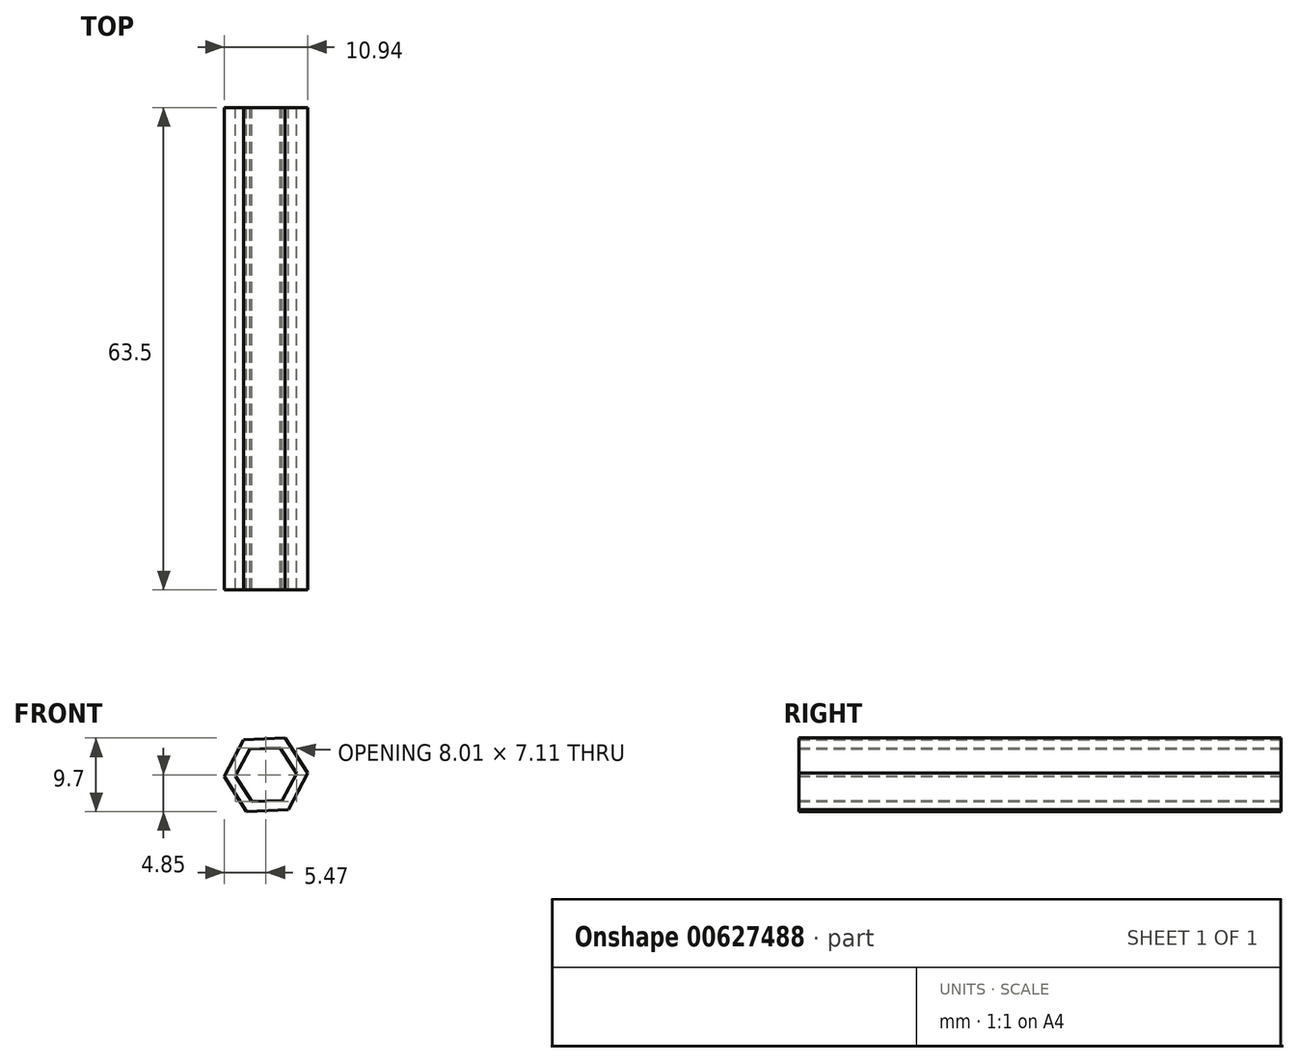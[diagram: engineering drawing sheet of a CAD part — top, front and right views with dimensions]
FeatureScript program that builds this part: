
annotation { "Feature Type Name" : "Feature", "Feature Type Description" : "" }
export const myFeature = defineFeature(function(context is Context, id is Id, definition is map)
    precondition{}
    {
        {
            var Q0;
            Q0=qCreatedBy(makeId("Front.planeOp"),FACE);
            var sketch = newSketch(context, id + "F0", { "sketchPlane" : qUnion([Q0])});
            skCircle(sketch, "E0.cCircle", {"center": v(0, 0) * mm, "radius": 3.47 * mm, "construction": true});
            skLineSegment(sketch, "E0.0", {"start": v(1.86, 3.55) * mm, "end": v(4, 0.16) * mm});
            skLineSegment(sketch, "E0.1", {"start": v(4, 0.16) * mm, "end": v(2.15, -3.39) * mm});
            skLineSegment(sketch, "E0.2", {"start": v(2.15, -3.39) * mm, "end": v(-1.86, -3.55) * mm});
            skLineSegment(sketch, "E0.3", {"start": v(-1.86, -3.55) * mm, "end": v(-4, -0.16) * mm});
            skLineSegment(sketch, "E0.4", {"start": v(-4, -0.16) * mm, "end": v(-2.15, 3.39) * mm});
            skLineSegment(sketch, "E0.5", {"start": v(-2.15, 3.39) * mm, "end": v(1.86, 3.55) * mm});
            skPoint(sketch, "E0.0.midPoint", {"position": v(2.93, 1.86) * mm});
            skCircle(sketch, "E1.cCircle", {"center": v(0, 0) * mm, "radius": 4.74 * mm, "construction": true});
            skLineSegment(sketch, "E1.0", {"start": v(2.54, 4.85) * mm, "end": v(5.47, 0.22) * mm});
            skLineSegment(sketch, "E1.1", {"start": v(5.47, 0.22) * mm, "end": v(2.93, -4.63) * mm});
            skLineSegment(sketch, "E1.2", {"start": v(2.93, -4.63) * mm, "end": v(-2.54, -4.85) * mm});
            skLineSegment(sketch, "E1.3", {"start": v(-2.54, -4.85) * mm, "end": v(-5.47, -0.22) * mm});
            skLineSegment(sketch, "E1.4", {"start": v(-5.47, -0.22) * mm, "end": v(-2.93, 4.63) * mm});
            skLineSegment(sketch, "E1.5", {"start": v(-2.93, 4.63) * mm, "end": v(2.54, 4.85) * mm});
            skPoint(sketch, "E1.0.midPoint", {"position": v(4, 2.54) * mm});
            skSolve(sketch);
        }
        {
            var Q0;
            Q0=makeQuery(id+"F0.imprint","IMPRINT",FACE,{"disambiguationData":[TD([[makeQuery(id+"F0.imprint","IMPRINT",EDGE,{"derivedFrom":sQuery(id+"F0.wireOp",EDGE,"E0.0")}),1.0]])]});
            extrude(context, id + "F1", {"entities" : qUnion([Q0]), "endBound" : BoundingType.SYMMETRIC, "depth" : 63.5 * mm, "offsetDistance" : 25.4 * mm});
        }
    });
